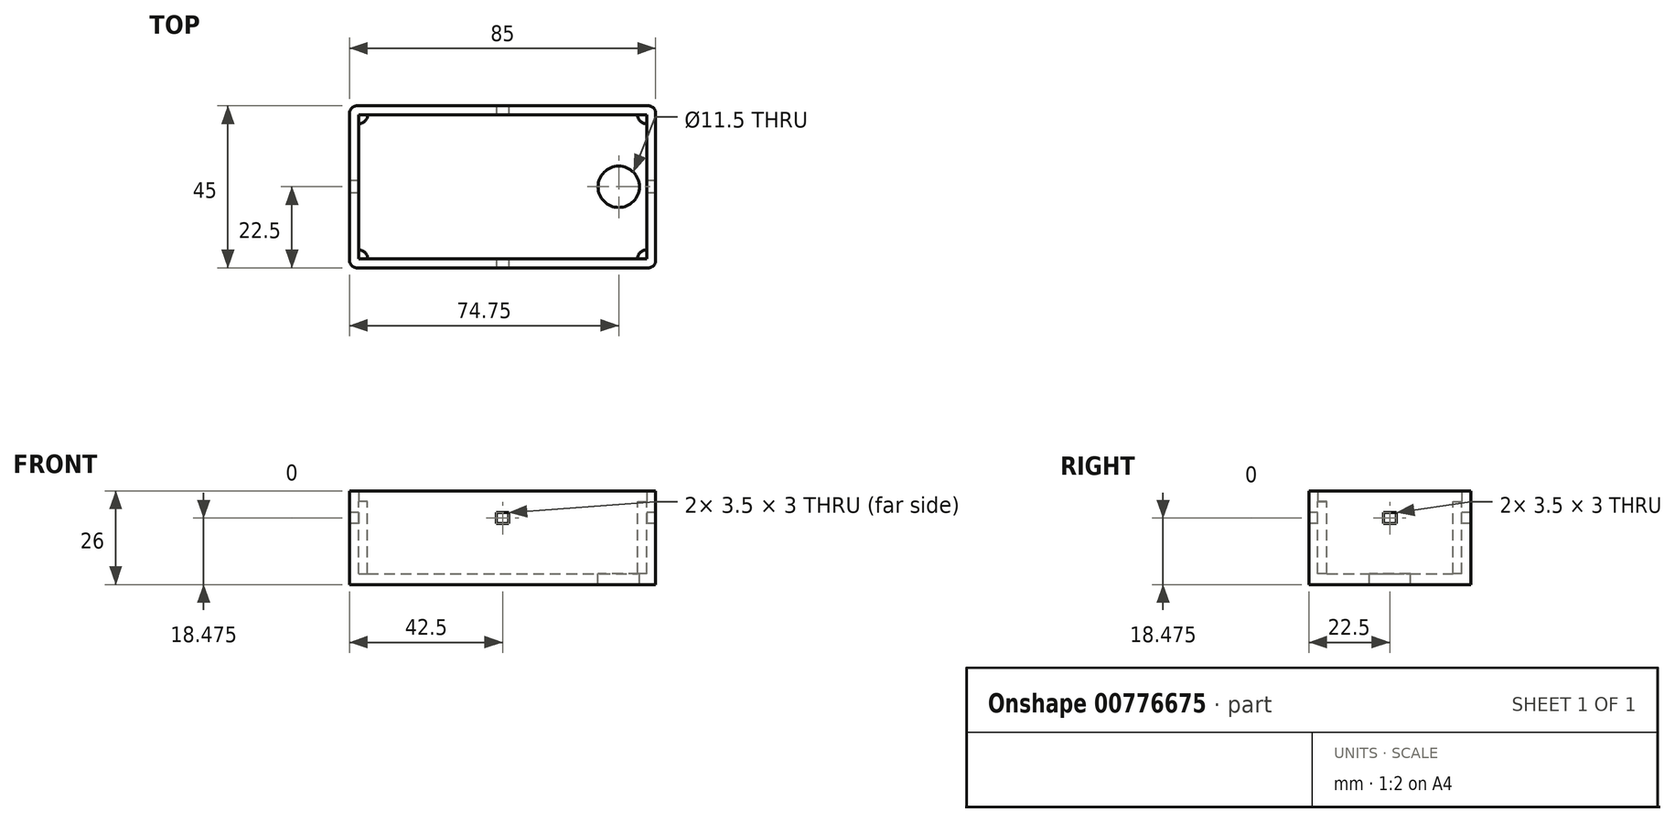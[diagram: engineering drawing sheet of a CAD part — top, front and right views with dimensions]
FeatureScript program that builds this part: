
annotation { "Feature Type Name" : "Feature", "Feature Type Description" : "" }
export const myFeature = defineFeature(function(context is Context, id is Id, definition is map)
    precondition{}
    {
        {
            var Q0;
            Q0=qCreatedBy(makeId("Top.planeOp"),FACE);
            var sketch = newSketch(context, id + "F0", { "sketchPlane" : qUnion([Q0])});
            skLineSegment(sketch, "E0.bottom", {"start": v(40, 20) * mm, "end": v(-40, 20) * mm});
            skLineSegment(sketch, "E0.top", {"start": v(40, -20) * mm, "end": v(-40, -20) * mm});
            skLineSegment(sketch, "E0.left", {"start": v(40, 20) * mm, "end": v(40, -20) * mm});
            skLineSegment(sketch, "E0.right", {"start": v(-40, 20) * mm, "end": v(-40, -20) * mm});
            skPoint(sketch, "E0.middle", {"position": v(0, 0) * mm});
            skLineSegment(sketch, "E1.bottom", {"start": v(42.5, 22.5) * mm, "end": v(-42.5, 22.5) * mm});
            skLineSegment(sketch, "E1.top", {"start": v(42.5, -22.5) * mm, "end": v(-42.5, -22.5) * mm});
            skLineSegment(sketch, "E1.left", {"start": v(42.5, 22.5) * mm, "end": v(42.5, -22.5) * mm});
            skLineSegment(sketch, "E1.right", {"start": v(-42.5, 22.5) * mm, "end": v(-42.5, -22.5) * mm});
            skSolve(sketch);
        }
        {
            var Q0;
            Q0=makeQuery(id+"F0.imprint","IMPRINT",FACE,{"disambiguationData":[TD([[makeQuery(id+"F0.imprint","IMPRINT",EDGE,{"derivedFrom":sQuery(id+"F0.wireOp",EDGE,"E0.bottom")}),-1.0]])]});
            var Q1;
            Q1=makeQuery(id+"F0.imprint","IMPRINT",FACE,{"disambiguationData":[TD([[makeQuery(id+"F0.imprint","IMPRINT",EDGE,{"derivedFrom":sQuery(id+"F0.wireOp",EDGE,"E0.bottom")}),1.0]])]});
            extrude(context, id + "F1", {"entities" : qUnion([Q0, Q1]), "depth" : 3 * mm, "offsetDistance" : 25 * mm});
        }
        {
            var Q0;
            Q0=makeQuery(id+"F0.imprint","IMPRINT",FACE,{"disambiguationData":[TD([[makeQuery(id+"F0.imprint","IMPRINT",EDGE,{"derivedFrom":sQuery(id+"F0.wireOp",EDGE,"E0.bottom")}),-1.0]])]});
            extrude(context, id + "F2", {"entities" : qUnion([Q0]), "operationType" : NewBodyOperationType.ADD, "depth" : 26 * mm, "offsetDistance" : 25 * mm});
        }
        {
            var Q0;
            Q0=makeQuery(id+"F2.opExtrude","CAP_FACE",FACE,{"disambiguationData":[OSD([sQuery(id+"F0.wireOp",EDGE,"E0.bottom"),sQuery(id+"F0.wireOp",EDGE,"E0.top"),sQuery(id+"F0.wireOp",EDGE,"E0.left"),sQuery(id+"F0.wireOp",EDGE,"E0.right"),sQuery(id+"F0.wireOp",EDGE,"E1.bottom"),sQuery(id+"F0.wireOp",EDGE,"E1.top"),sQuery(id+"F0.wireOp",EDGE,"E1.left"),sQuery(id+"F0.wireOp",EDGE,"E1.right")])],"isStart":false});
            cPlane(context, id + "F3", {"entities" : qUnion([Q0]), "cplaneType" : CPlaneType.OFFSET, "offset" : 3 * mm, "oppositeDirection" : true, "width" : 150 * mm, "height" : 150 * mm});
        }
        {
            var Q0;
            Q0=qCreatedBy(id+"F3.planeOp",FACE);
            var sketch = newSketch(context, id + "F4", { "sketchPlane" : qUnion([Q0])});
            skCircle(sketch, "E2", {"center": v(-40, -20) * mm, "radius": 2.5 * mm});
            skCircle(sketch, "E3", {"center": v(-40, 20) * mm, "radius": 2.5 * mm});
            skCircle(sketch, "E4", {"center": v(40, 20) * mm, "radius": 2.5 * mm});
            skCircle(sketch, "E5", {"center": v(40, -20) * mm, "radius": 2.5 * mm});
            skSolve(sketch);
        }
        {
            var Q0;
            Q0=makeQuery(id+"F4.imprint","IMPRINT",FACE,{"disambiguationData":[TD([[makeQuery(id+"F4.imprint","IMPRINT",EDGE,{"derivedFrom":sQuery(id+"F4.wireOp",EDGE,"E3")}),1.0]])]});
            var Q1;
            Q1=makeQuery(id+"F4.imprint","IMPRINT",FACE,{"disambiguationData":[TD([[makeQuery(id+"F4.imprint","IMPRINT",EDGE,{"derivedFrom":sQuery(id+"F4.wireOp",EDGE,"E4")}),1.0]])]});
            var Q2;
            Q2=makeQuery(id+"F4.imprint","IMPRINT",FACE,{"disambiguationData":[TD([[makeQuery(id+"F4.imprint","IMPRINT",EDGE,{"derivedFrom":sQuery(id+"F4.wireOp",EDGE,"E5")}),1.0]])]});
            var Q3;
            Q3=makeQuery(id+"F4.imprint","IMPRINT",FACE,{"disambiguationData":[TD([[makeQuery(id+"F4.imprint","IMPRINT",EDGE,{"derivedFrom":sQuery(id+"F4.wireOp",EDGE,"E2")}),1.0]])]});
            extrude(context, id + "F5", {"entities" : qUnion([Q0, Q1, Q2, Q3]), "operationType" : NewBodyOperationType.ADD, "endBound" : BoundingType.UP_TO_NEXT, "oppositeDirection" : true, "depth" : 25 * mm, "offsetDistance" : 25 * mm});
        }
        {
            var Q0;
            {var subQ0=sQuery(id+"F0.wireOp",EDGE,"E1.right");Q0=makeQuery(id+"F2.boolean.opBoolean","MERGE",FACE,{"derivedFrom":[makeQuery(id+"F1.opExtrude","SWEPT_FACE",FACE,{"disambiguationData":[OSD([subQ0])]}),makeQuery(id+"F2.opExtrude","SWEPT_FACE",FACE,{"disambiguationData":[OSD([subQ0])]})]});}
            var sketch = newSketch(context, id + "F6", { "sketchPlane" : qUnion([Q0])});
            skLineSegment(sketch, "E6.bottom", {"start": v(-1.75, 16.98) * mm, "end": v(1.75, 16.98) * mm});
            skLineSegment(sketch, "E6.top", {"start": v(-1.75, 19.98) * mm, "end": v(1.75, 19.98) * mm});
            skLineSegment(sketch, "E6.left", {"start": v(-1.75, 16.98) * mm, "end": v(-1.75, 19.98) * mm});
            skLineSegment(sketch, "E6.right", {"start": v(1.75, 16.98) * mm, "end": v(1.75, 19.98) * mm});
            skSolve(sketch);
        }
        {
            var Q0;
            Q0=makeQuery(id+"F6.imprint","IMPRINT",FACE,{"disambiguationData":[TD([[makeQuery(id+"F6.imprint","IMPRINT",EDGE,{"derivedFrom":sQuery(id+"F6.wireOp",EDGE,"E6.bottom")}),1.0]])]});
            extrude(context, id + "F7", {"entities" : qUnion([Q0]), "operationType" : NewBodyOperationType.REMOVE, "endBound" : BoundingType.THROUGH_ALL, "oppositeDirection" : true, "depth" : 25 * mm, "offsetDistance" : 25 * mm});
        }
        {
            var Q0;
            Q0=qCreatedBy(makeId("Front.planeOp"),FACE);
            var sketch = newSketch(context, id + "F8", { "sketchPlane" : qUnion([Q0])});
            skLineSegment(sketch, "E7.bottom", {"start": v(-1.75, 16.98) * mm, "end": v(1.75, 16.98) * mm});
            skLineSegment(sketch, "E7.top", {"start": v(-1.75, 19.98) * mm, "end": v(1.75, 19.98) * mm});
            skLineSegment(sketch, "E7.left", {"start": v(-1.75, 16.98) * mm, "end": v(-1.75, 19.98) * mm});
            skLineSegment(sketch, "E7.right", {"start": v(1.75, 16.98) * mm, "end": v(1.75, 19.98) * mm});
            skSolve(sketch);
        }
        {
            var Q0;
            Q0=makeQuery(id+"F8.imprint","IMPRINT",FACE,{"disambiguationData":[TD([[makeQuery(id+"F8.imprint","IMPRINT",EDGE,{"derivedFrom":sQuery(id+"F8.wireOp",EDGE,"E7.bottom")}),1.0]])]});
            extrude(context, id + "F9", {"entities" : qUnion([Q0]), "operationType" : NewBodyOperationType.REMOVE, "endBound" : BoundingType.SYMMETRIC, "oppositeDirection" : true, "depth" : 60 * mm, "offsetDistance" : 25 * mm});
        }
        {
            var Q0;
            {var subQ0=sQuery(id+"F0.wireOp",EDGE,"E1.right");var subQ1=sQuery(id+"F0.wireOp",EDGE,"E1.top");Q0=makeQuery(id+"F2.boolean.opBoolean","MERGE",EDGE,{"derivedFrom":[makeQuery(id+"F1.opExtrude","SWEPT_EDGE",EDGE,{"disambiguationData":[OSD([subQ1,subQ0])]}),makeQuery(id+"F2.opExtrude","SWEPT_EDGE",EDGE,{"disambiguationData":[OSD([subQ1,subQ0])]})]});}
            var Q1;
            {var subQ0=sQuery(id+"F0.wireOp",EDGE,"E1.left");var subQ1=sQuery(id+"F0.wireOp",EDGE,"E1.top");Q1=makeQuery(id+"F2.boolean.opBoolean","MERGE",EDGE,{"derivedFrom":[makeQuery(id+"F1.opExtrude","SWEPT_EDGE",EDGE,{"disambiguationData":[OSD([subQ1,subQ0])]}),makeQuery(id+"F2.opExtrude","SWEPT_EDGE",EDGE,{"disambiguationData":[OSD([subQ1,subQ0])]})]});}
            var Q2;
            {var subQ0=sQuery(id+"F0.wireOp",EDGE,"E1.right");var subQ1=sQuery(id+"F0.wireOp",EDGE,"E1.bottom");Q2=makeQuery(id+"F2.boolean.opBoolean","MERGE",EDGE,{"derivedFrom":[makeQuery(id+"F1.opExtrude","SWEPT_EDGE",EDGE,{"disambiguationData":[OSD([subQ1,subQ0])]}),makeQuery(id+"F2.opExtrude","SWEPT_EDGE",EDGE,{"disambiguationData":[OSD([subQ1,subQ0])]})]});}
            var Q3;
            {var subQ0=sQuery(id+"F0.wireOp",EDGE,"E1.left");var subQ1=sQuery(id+"F0.wireOp",EDGE,"E1.bottom");Q3=makeQuery(id+"F2.boolean.opBoolean","MERGE",EDGE,{"derivedFrom":[makeQuery(id+"F1.opExtrude","SWEPT_EDGE",EDGE,{"disambiguationData":[OSD([subQ1,subQ0])]}),makeQuery(id+"F2.opExtrude","SWEPT_EDGE",EDGE,{"disambiguationData":[OSD([subQ1,subQ0])]})]});}
            fillet(context, id + "F10", {"entities" : qUnion([Q0, Q1, Q2, Q3]), "radius" : 2 * mm, "tangentPropagation" : true, "allowEdgeOverflow" : false});
        }
        {
            var Q0;
            Q0=makeQuery(id+"F1.opExtrude","CAP_FACE",FACE,{"disambiguationData":[OSD([sQuery(id+"F0.wireOp",EDGE,"E1.bottom"),sQuery(id+"F0.wireOp",EDGE,"E1.top"),sQuery(id+"F0.wireOp",EDGE,"E1.left"),sQuery(id+"F0.wireOp",EDGE,"E1.right")])],"isStart":false});
            var sketch = newSketch(context, id + "F11", { "sketchPlane" : qUnion([Q0])});
            skCircle(sketch, "E8", {"center": v(32.25, 0) * mm, "radius": 5.75 * mm});
            skSolve(sketch);
        }
        {
            var Q0;
            Q0=makeQuery(id+"F11.imprint","IMPRINT",FACE,{"disambiguationData":[TD([[makeQuery(id+"F11.imprint","IMPRINT",EDGE,{"derivedFrom":sQuery(id+"F11.wireOp",EDGE,"E8")}),1.0]])]});
            extrude(context, id + "F12", {"entities" : qUnion([Q0]), "operationType" : NewBodyOperationType.REMOVE, "endBound" : BoundingType.UP_TO_NEXT, "oppositeDirection" : true, "depth" : 25 * mm, "offsetDistance" : 25 * mm});
        }
    });
